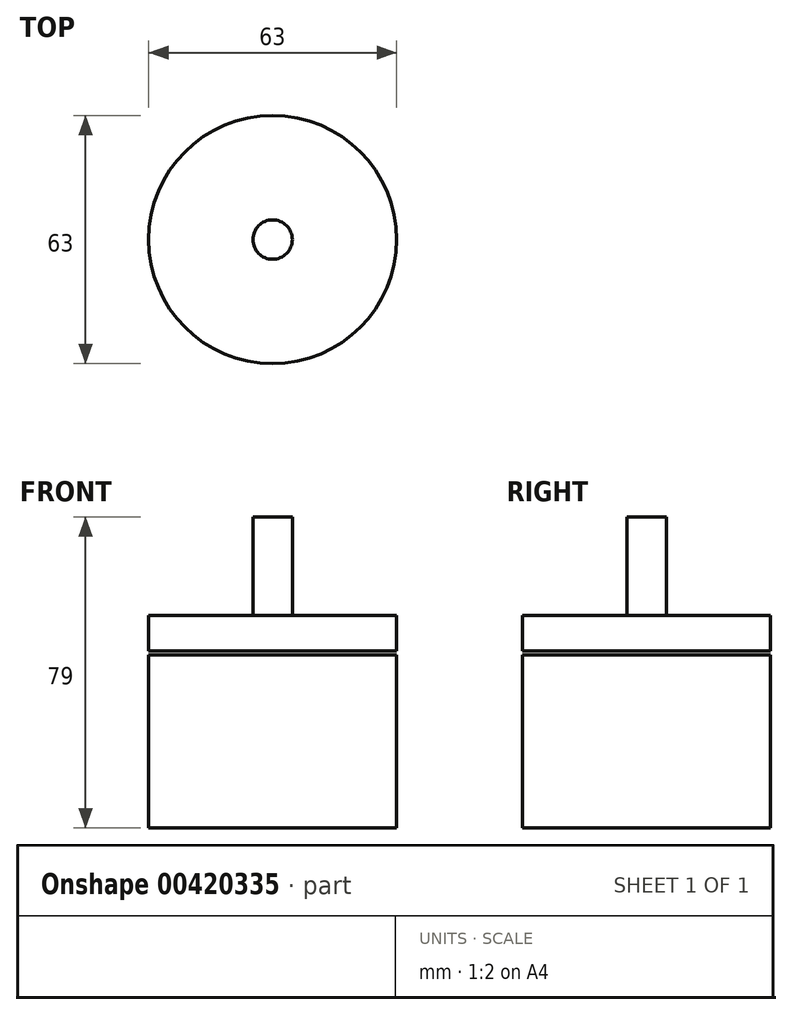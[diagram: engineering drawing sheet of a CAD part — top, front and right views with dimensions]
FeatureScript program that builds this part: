
annotation { "Feature Type Name" : "Feature", "Feature Type Description" : "" }
export const myFeature = defineFeature(function(context is Context, id is Id, definition is map)
    precondition{}
    {
        {
            var Q0;
            Q0=qCreatedBy(makeId("Top.planeOp"),FACE);
            var sketch = newSketch(context, id + "F0", { "sketchPlane" : qUnion([Q0])});
            skCircle(sketch, "E0", {"center": v(0, 0) * mm, "radius": 31.5 * mm});
            skSolve(sketch);
        }
        {
            var Q0;
            Q0=qSketchRegion(id+"F0",true);
            extrude(context, id + "F1", {"entities" : qUnion([Q0]), "depth" : 44 * mm});
        }
        {
            var Q0;
            Q0=makeQuery(id+"F1.opExtrude","CAP_FACE",FACE,{"disambiguationData":[OSD([sQuery(id+"F0.wireOp",EDGE,"E0")])],"isStart":false});
            var sketch = newSketch(context, id + "F2", { "sketchPlane" : qUnion([Q0])});
            skCircle(sketch, "E1", {"center": v(0, 0) * mm, "radius": 31.5 * mm});
            skSolve(sketch);
        }
        {
            var Q0;
            Q0=qSketchRegion(id+"F2",true);
            extrude(context, id + "F3", {"entities" : qUnion([Q0]), "operationType" : NewBodyOperationType.ADD, "depth" : 10 * mm, "hasSecondDirection" : true, "secondDirectionOppositeDirection" : false, "secondDirectionDepth" : 1 * mm});
        }
        {
            var Q0;
            Q0=makeQuery(id+"F3.opExtrude","CAP_FACE",FACE,{"disambiguationData":[OSD([sQuery(id+"F2.wireOp",EDGE,"E1")])],"isStart":false});
            var sketch = newSketch(context, id + "F4", { "sketchPlane" : qUnion([Q0])});
            skCircle(sketch, "E2", {"center": v(0, 0) * mm, "radius": 5 * mm});
            skSolve(sketch);
        }
        {
            var Q0;
            Q0=qSketchRegion(id+"F4",true);
            extrude(context, id + "F5", {"entities" : qUnion([Q0]), "operationType" : NewBodyOperationType.ADD, "depth" : 25 * mm});
        }
    });
